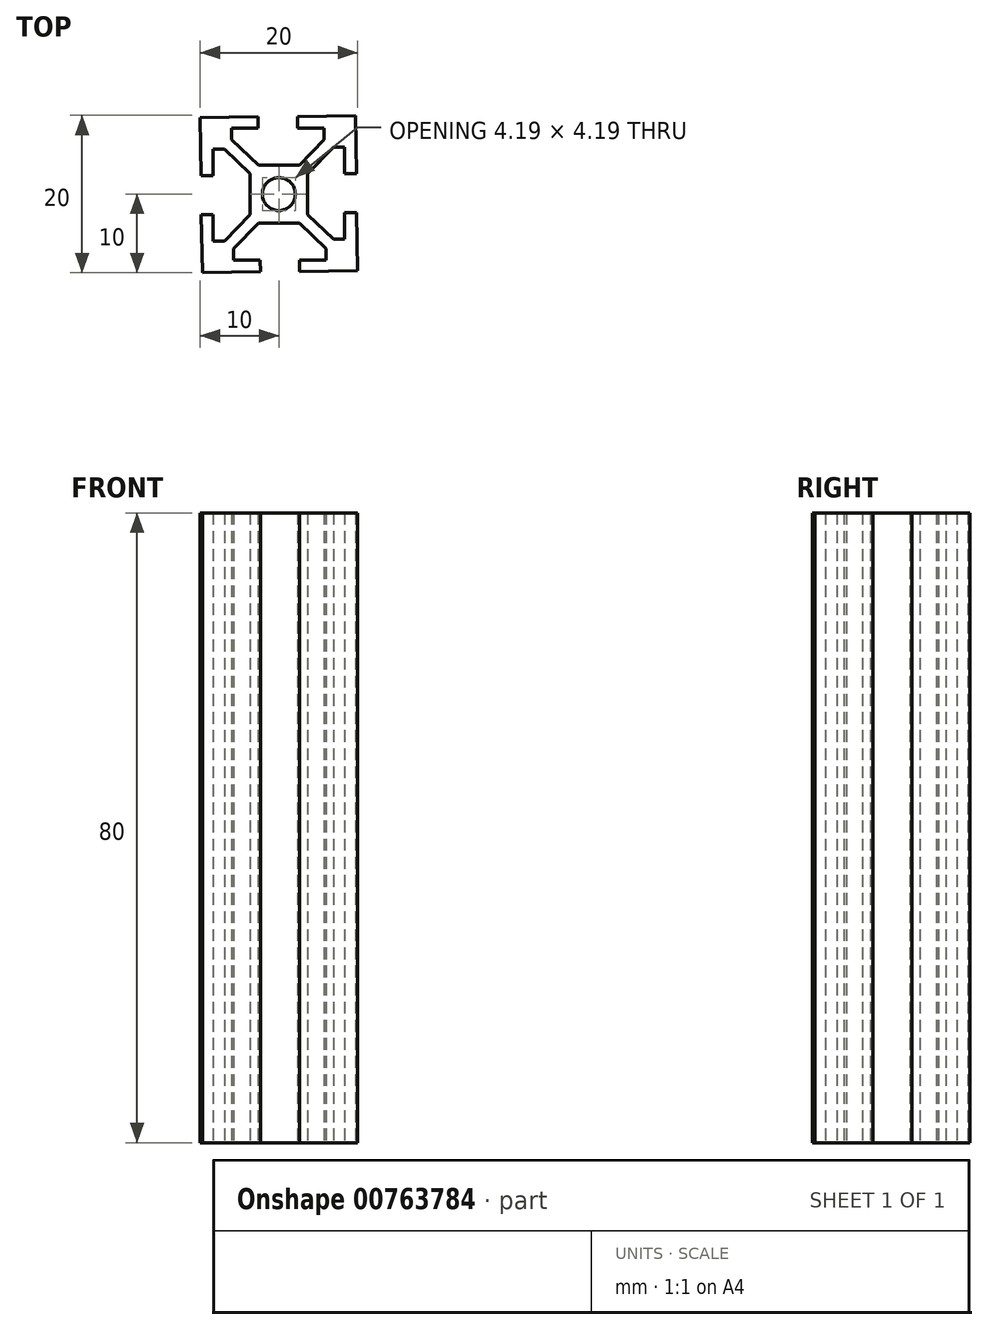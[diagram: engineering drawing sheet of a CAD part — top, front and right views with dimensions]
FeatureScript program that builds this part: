
annotation { "Feature Type Name" : "Feature", "Feature Type Description" : "" }
export const myFeature = defineFeature(function(context is Context, id is Id, definition is map)
    precondition{}
    {
        {
            var Q0;
            Q0=qCreatedBy(makeId("Top.planeOp"),FACE);
            var sketch = newSketch(context, id + "F0", { "sketchPlane" : qUnion([Q0])});
            skPoint(sketch, "E0.middle", {"position": v(0, 0) * mm});
            skLineSegment(sketch, "E1", {"start": v(-2.6, 3.65) * mm, "end": v(-6, 6.92) * mm});
            skLineSegment(sketch, "E2", {"start": v(-6, 6.92) * mm, "end": v(-6, 8.35) * mm});
            skLineSegment(sketch, "E3", {"start": v(-6, 8.35) * mm, "end": v(-2.63, 8.35) * mm});
            skLineSegment(sketch, "E4", {"start": v(-2.63, 8.35) * mm, "end": v(-2.63, 9.85) * mm});
            skLineSegment(sketch, "E5", {"start": v(-2.63, 9.85) * mm, "end": v(-10, 9.71) * mm});
            skLineSegment(sketch, "E6", {"start": v(-9.85, 2.34) * mm, "end": v(-8.35, 2.37) * mm});
            skLineSegment(sketch, "E7", {"start": v(-8.35, 2.37) * mm, "end": v(-8.35, 5.74) * mm});
            skLineSegment(sketch, "E8", {"start": v(-8.35, 5.74) * mm, "end": v(-6.92, 5.74) * mm});
            skLineSegment(sketch, "E9", {"start": v(-6.92, 5.74) * mm, "end": v(-3.65, 2.6) * mm});
            skLineSegment(sketch, "E10", {"start": v(-3.65, 2.6) * mm, "end": v(-3.65, 0) * mm});
            skLineSegment(sketch, "E11", {"start": v(0, 3.65) * mm, "end": v(-2.6, 3.65) * mm});
            skLineSegment(sketch, "E12", {"start": v(-1.75, 3.65) * mm, "end": v(-1.75, 8.35) * mm, "construction": true});
            skLineSegment(sketch, "E13", {"start": v(-3.65, 0.65) * mm, "end": v(-8.35, 0.65) * mm, "construction": true});
            skLineSegment(sketch, "E14", {"start": v(-9.85, 2.34) * mm, "end": v(-10, 9.71) * mm});
            skLineSegment(sketch, "E15", {"start": v(0, 9.9) * mm, "end": v(0, 13) * mm, "construction": true});
            skLineSegment(sketch, "E16", {"start": v(-4.9, 3.79) * mm, "end": v(-3.86, 4.87) * mm, "construction": true});
            skLineSegment(sketch, "E17", {"start": v(0, 13) * mm, "end": v(-10, 12.81) * mm, "construction": true});
            skLineSegment(sketch, "E18", {"start": v(-14.91, 9.71) * mm, "end": v(-14.72, -0.29) * mm, "construction": true});
            skLineSegment(sketch, "E19", {"start": v(-14.72, -0.29) * mm, "end": v(-18.94, -0.37) * mm, "construction": true});
            skArc(sketch, "E20", {"start": v(0, 2.1) * mm, "mid": v(-1.48, 1.48) * mm, "end": v(-2.1, 0) * mm});
            skLineSegment(sketch, "E21", {"start": v(0, 2.1) * mm, "end": v(0, 3.65) * mm});
            skLineSegment(sketch, "E22", {"start": v(-2.1, 0) * mm, "end": v(-3.65, 0) * mm});
            skLineSegment(sketch, "E23", {"start": v(0, 2.1) * mm, "end": v(0, 0) * mm, "construction": true});
            skLineSegment(sketch, "E24", {"start": v(0, 0) * mm, "end": v(-2.1, 0) * mm, "construction": true});
            skSolve(sketch);
        }
        {
            var Q0;
            Q0=makeQuery(id+"F0.imprint","IMPRINT",FACE,{"disambiguationData":[TD([[makeQuery(id+"F0.imprint","IMPRINT",EDGE,{"derivedFrom":sQuery(id+"F0.wireOp",EDGE,"E1")}),1.0]])]});
            extrude(context, id + "F1", {"entities" : qUnion([Q0]), "depth" : 80 * mm, "offsetDistance" : 25 * mm});
        }
        {
            var Q0;
            Q0=makeQuery(id+"F1.opExtrude","SWEPT_FACE",FACE,{"disambiguationData":[OSD([sQuery(id+"F0.wireOp",EDGE,"E21")])]});
            var sketch = newSketch(context, id + "F2", { "sketchPlane" : qUnion([Q0])});
            skLineSegment(sketch, "E25", {"start": v(0, 0) * mm, "end": v(0, 1.38) * mm, "construction": true});
            skSolve(sketch);
        }
        {
            var Q0;
            Q0=makeQuery(id+"F1.opExtrude","SWEPT_BODY",BODY,{"disambiguationData":[OSD([sQuery(id+"F0.wireOp",EDGE,"E1"),sQuery(id+"F0.wireOp",EDGE,"E2"),sQuery(id+"F0.wireOp",EDGE,"E3"),sQuery(id+"F0.wireOp",EDGE,"E4"),sQuery(id+"F0.wireOp",EDGE,"E6"),sQuery(id+"F0.wireOp",EDGE,"E7"),sQuery(id+"F0.wireOp",EDGE,"E8"),sQuery(id+"F0.wireOp",EDGE,"E9"),sQuery(id+"F0.wireOp",EDGE,"E10"),sQuery(id+"F0.wireOp",EDGE,"E11"),sQuery(id+"F0.wireOp",EDGE,"E14"),sQuery(id+"F0.wireOp",EDGE,"E5"),sQuery(id+"F0.wireOp",EDGE,"E20"),sQuery(id+"F0.wireOp",EDGE,"E21"),sQuery(id+"F0.wireOp",EDGE,"E22")])]});
            var Q1;
            Q1=sQuery(id+"F2.wireOp",EDGE,"E25");
            circularPattern(context, id + "F3", {"operationType" : NewBodyOperationType.ADD, "entities" : qUnion([Q0]), "axis" : qUnion([Q1]), "angle" : 360 * degree, "instanceCount" : 4, "equalSpace" : true});
        }
    });
